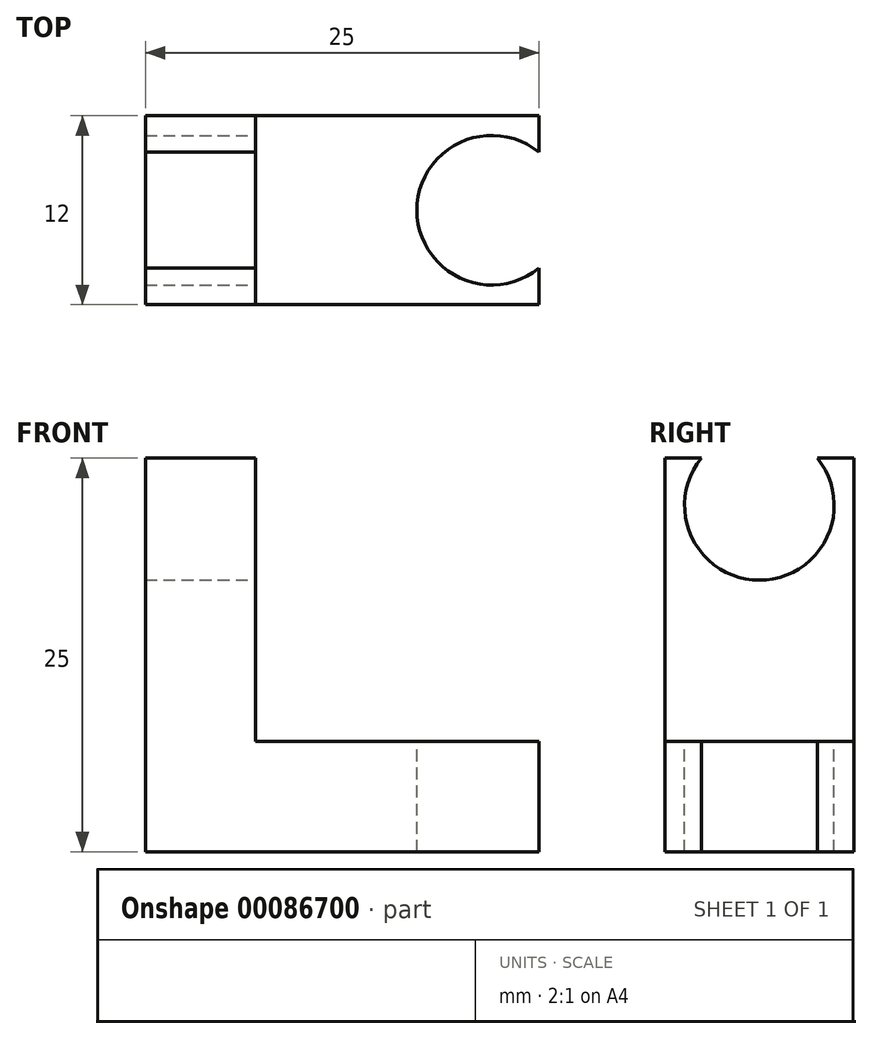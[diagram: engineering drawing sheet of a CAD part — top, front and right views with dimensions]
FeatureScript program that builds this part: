
annotation { "Feature Type Name" : "Feature", "Feature Type Description" : "" }
export const myFeature = defineFeature(function(context is Context, id is Id, definition is map)
    precondition{}
    {
        {
            var Q0;
            Q0=qCreatedBy(makeId("Front.planeOp"),FACE);
            var sketch = newSketch(context, id + "F0", { "sketchPlane" : qUnion([Q0])});
            skLineSegment(sketch, "E0", {"start": v(0, 25) * mm, "end": v(0, 0) * mm});
            skLineSegment(sketch, "E1", {"start": v(0, 0) * mm, "end": v(25, 0) * mm});
            skLineSegment(sketch, "E2", {"start": v(25, 0) * mm, "end": v(25, 7) * mm});
            skLineSegment(sketch, "E3", {"start": v(25, 7) * mm, "end": v(7, 7) * mm});
            skLineSegment(sketch, "E4", {"start": v(7, 7) * mm, "end": v(7, 25) * mm});
            skLineSegment(sketch, "E5", {"start": v(7, 25) * mm, "end": v(0, 25) * mm});
            skSolve(sketch);
        }
        {
            var Q0;
            Q0=makeQuery(id+"F0.imprint","IMPRINT",FACE,{"disambiguationData":[TD([[makeQuery(id+"F0.imprint","IMPRINT",EDGE,{"derivedFrom":sQuery(id+"F0.wireOp",EDGE,"E0")}),1.0]])]});
            extrude(context, id + "F1", {"entities" : qUnion([Q0]), "endBound" : BoundingType.SYMMETRIC, "depth" : 12 * mm});
        }
        {
            var Q0;
            Q0=makeQuery(id+"F1.opExtrude","SWEPT_FACE",FACE,{"disambiguationData":[OSD([sQuery(id+"F0.wireOp",EDGE,"E3")])]});
            var sketch = newSketch(context, id + "F2", { "sketchPlane" : qUnion([Q0])});
            skCircle(sketch, "E6", {"center": v(22, 0) * mm, "radius": 4.75 * mm});
            skSolve(sketch);
        }
        {
            var Q0;
            {var subQ0=sQuery(id+"F2.wireOp",EDGE,"E6");var subQ1=makeQuery(id+"F1.opExtrude","SWEPT_EDGE",EDGE,{"disambiguationData":[OSD([sQuery(id+"F0.wireOp",EDGE,"E2"),sQuery(id+"F0.wireOp",EDGE,"E3")])]});var subQ2=makeQuery(id+"F2.imprint","INTERSECT",VERTEX,{"disambiguationData":[OD(0.0)],"derivedFrom":[subQ1,subQ0]});Q0=makeQuery(id+"F2.imprint","IMPRINT",FACE,{"disambiguationData":[TD([[makeQuery(id+"F2.imprint","IMPRINT",EDGE,{"disambiguationData":[TD([[subQ2,1.0]])],"derivedFrom":subQ0}),1.0]])]});}
            var Q1;
            {var subQ0=sQuery(id+"F2.wireOp",EDGE,"E6");var subQ1=makeQuery(id+"F1.opExtrude","SWEPT_EDGE",EDGE,{"disambiguationData":[OSD([sQuery(id+"F0.wireOp",EDGE,"E2"),sQuery(id+"F0.wireOp",EDGE,"E3")])]});var subQ2=makeQuery(id+"F2.imprint","INTERSECT",VERTEX,{"disambiguationData":[OD(0.0)],"derivedFrom":[subQ1,subQ0]});Q1=makeQuery(id+"F2.imprint","IMPRINT",FACE,{"disambiguationData":[TD([[makeQuery(id+"F2.imprint","IMPRINT",EDGE,{"disambiguationData":[TD([[subQ2,-1.0]])],"derivedFrom":subQ0}),1.0]])]});}
            var Q2;
            Q2=sQuery(id+"F2.wireOp",EDGE,"E6");
            extrude(context, id + "F3", {"entities" : qUnion([Q0, Q1]), "operationType" : NewBodyOperationType.REMOVE, "surfaceEntities" : qUnion([Q2]), "endBound" : BoundingType.THROUGH_ALL, "oppositeDirection" : true, "depth" : 25 * mm});
        }
        {
            var Q0;
            Q0=makeQuery(id+"F1.opExtrude","SWEPT_FACE",FACE,{"disambiguationData":[OSD([sQuery(id+"F0.wireOp",EDGE,"E4")])]});
            var sketch = newSketch(context, id + "F4", { "sketchPlane" : qUnion([Q0])});
            skCircle(sketch, "E7", {"center": v(0, 22) * mm, "radius": 4.75 * mm});
            skSolve(sketch);
        }
        {
            var Q0;
            Q0=qSketchRegion(id+"F4",true);
            extrude(context, id + "F5", {"entities" : qUnion([Q0]), "operationType" : NewBodyOperationType.REMOVE, "oppositeDirection" : true, "depth" : 25 * mm});
        }
    });
